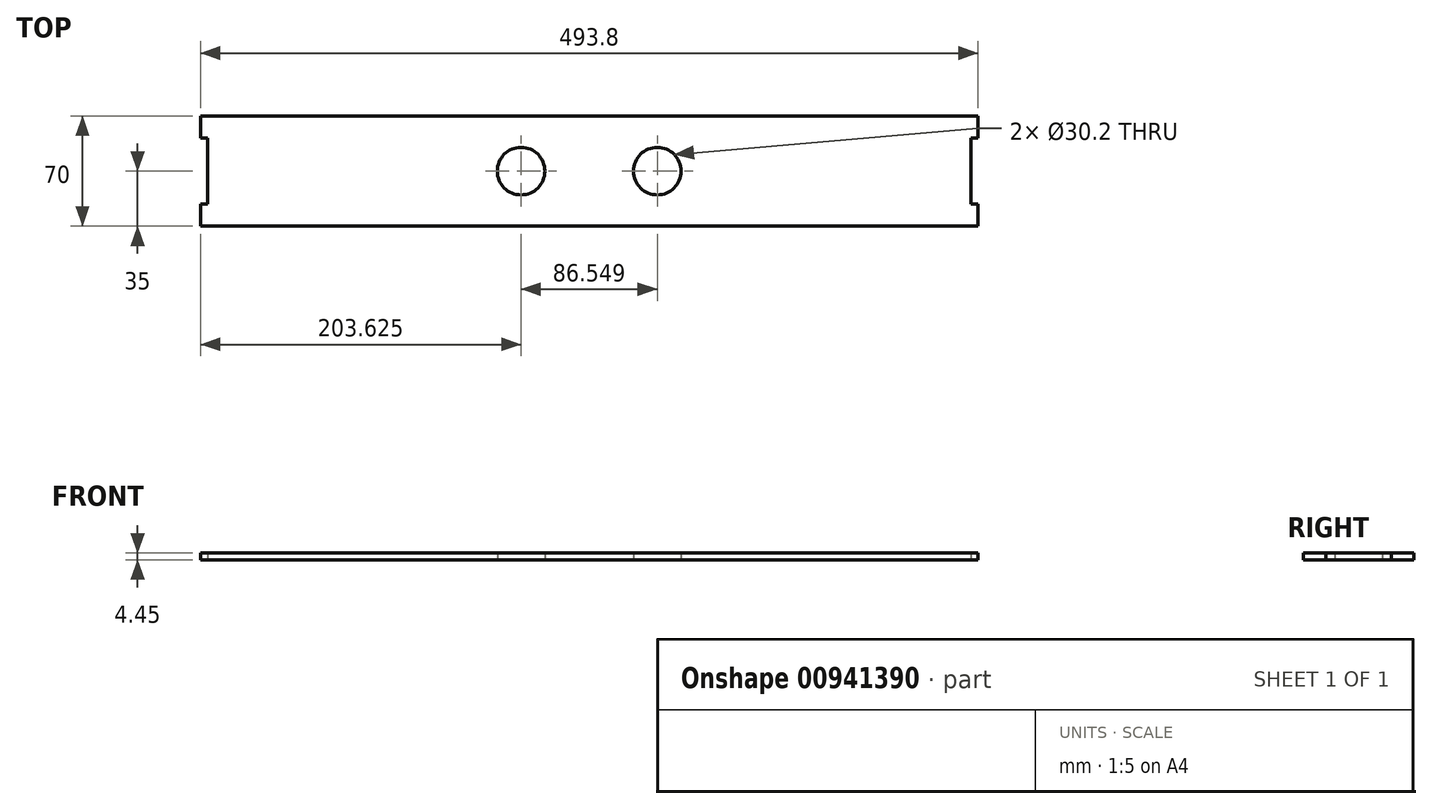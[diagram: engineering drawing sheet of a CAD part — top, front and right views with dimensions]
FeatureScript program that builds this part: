
annotation { "Feature Type Name" : "Feature", "Feature Type Description" : "" }
export const myFeature = defineFeature(function(context is Context, id is Id, definition is map)
    precondition{}
    {
        {
            var Q0;
            Q0=qCreatedBy(makeId("Top.planeOp"),FACE);
            var sketch = newSketch(context, id + "F0", { "sketchPlane" : qUnion([Q0])});
            skLineSegment(sketch, "E0.bottom", {"start": v(242.45, -35) * mm, "end": v(-242.45, -35) * mm});
            skLineSegment(sketch, "E0.top", {"start": v(242.45, 35) * mm, "end": v(-242.45, 35) * mm});
            skPoint(sketch, "E0.middle", {"position": v(0, 0) * mm});
            skPoint(sketch, "E1.middle", {"position": v(-242.45, 0) * mm});
            skPoint(sketch, "E1.right.end.orphan", {"position": v(-246.9, 20.89) * mm});
            skPoint(sketch, "E2.orphan", {"position": v(-246.9, -21.89) * mm});
            skLineSegment(sketch, "E3", {"start": v(242.45, 21.89) * mm, "end": v(242.45, -21.89) * mm});
            skLineSegment(sketch, "E4", {"start": v(-242.45, 21.89) * mm, "end": v(-242.45, -21.89) * mm});
            skLineSegment(sketch, "E5.bottom", {"start": v(-242.45, 35) * mm, "end": v(-246.9, 35) * mm});
            skLineSegment(sketch, "E5.top", {"start": v(-242.45, 20.89) * mm, "end": v(-246.9, 20.89) * mm});
            skLineSegment(sketch, "E5.right", {"start": v(-246.9, 35) * mm, "end": v(-246.9, 20.89) * mm});
            skPoint(sketch, "E1.top.start.orphan", {"position": v(-238, 21.89) * mm});
            skPoint(sketch, "E1.bottom.start.orphan", {"position": v(-238, -20.89) * mm});
            skLineSegment(sketch, "E6.MirrorCS", {"start": v(242.45, 20.89) * mm, "end": v(246.9, 20.89) * mm});
            skLineSegment(sketch, "E7.MirrorCS", {"start": v(246.9, 35) * mm, "end": v(246.9, 20.89) * mm});
            skLineSegment(sketch, "E8.MirrorCS", {"start": v(242.45, 35) * mm, "end": v(246.9, 35) * mm});
            skLineSegment(sketch, "E9.MirrorCS", {"start": v(-242.45, -20.89) * mm, "end": v(-246.9, -20.89) * mm});
            skLineSegment(sketch, "E10.MirrorCS", {"start": v(-246.9, -35) * mm, "end": v(-246.9, -20.89) * mm});
            skLineSegment(sketch, "E11.MirrorCS", {"start": v(-242.45, -35) * mm, "end": v(-246.9, -35) * mm});
            skLineSegment(sketch, "E12.MirrorCS", {"start": v(242.45, -20.89) * mm, "end": v(246.9, -20.89) * mm});
            skLineSegment(sketch, "E13.MirrorCS", {"start": v(242.45, -35) * mm, "end": v(246.9, -35) * mm});
            skLineSegment(sketch, "E14.MirrorCS", {"start": v(246.9, -35) * mm, "end": v(246.9, -20.89) * mm});
            skPoint(sketch, "E15.MirrorCS.end.orphan", {"position": v(238, 21.89) * mm});
            skPoint(sketch, "E15.MirrorCS.start.orphan", {"position": v(238, -20.89) * mm});
            skCircle(sketch, "E16", {"center": v(-43.27, 0) * mm, "radius": 15.1 * mm});
            skCircle(sketch, "E17.MirrorC", {"center": v(43.27, 0) * mm, "radius": 15.1 * mm});
            skSolve(sketch);
        }
        {
            var Q0;
            Q0=makeQuery(id+"F0.imprint","IMPRINT",FACE,{"disambiguationData":[TD([[makeQuery(id+"F0.imprint","IMPRINT",EDGE,{"derivedFrom":sQuery(id+"F0.wireOp",EDGE,"E0.bottom")}),-1.0]])]});
            extrude(context, id + "F1", {"entities" : qUnion([Q0]), "depth" : 4.45 * mm, "offsetDistance" : 25 * mm});
        }
    });
